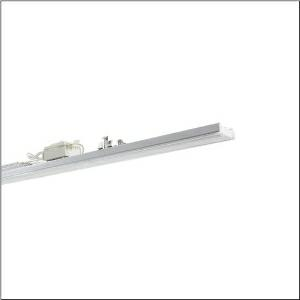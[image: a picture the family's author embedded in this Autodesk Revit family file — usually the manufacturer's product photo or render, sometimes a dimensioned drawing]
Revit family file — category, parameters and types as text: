
# Revit family: licross_r__21_recessed_mo_52te12dv4dxg_0a71
name_source: partatom
category: Lighting Fixtures
units: mm (PartAtom-declared; Revit-internal decimal feet)

## family parameters
Cut with Voids When Loaded = No
Host = Face
Light Source = No
Part Type = Normal
Room Calculation Point = No
Round Connector Dimension = Use Diameter
Shared = No

## types (1)
- --- (1 x LED, 13000 lm, 71 W, 4000K)
    Apparent Load = 71 VA
    CIE Flux Codes = 72 92 99 100 100
    Color Rendering = 80
    Color Temperature = 4000K
    Default Elevation = 1800 mm
    Description = Licross® 21 Recessed MO, luminaire insert, of sheet steel, galvanised, coil coated, white, length: 2.250mm, width: 66mm, height: 67mm, LED rated luminous flux: 13.000lm, light colour: 840, control gear: DALI 2, with plug, 5-pole, with phase selection, mains connection: 220..240V, AC, 50/60Hz, rated input power: 71W, halogen-free wiring, primary optical cover: cover, of PMMA, light emission: direct distribution, primary light characteristic: symmetric, protection rating (complete): IP54, insulation class (complete): insulation class I (protective earthing), certification: CE, ENEC, VDE, UKCA, protection symbol: D if used in an environment with non-conductive dust loads with corresponding accessories, impact resistance: IK06, permissible ambient temperature for indoor applications: -25..+35°C, corresponds to IFS (International Featured Standards) requirements for safety and quality in the food industry, reducing of maximum allowable ambient temperature of 5°C with ceiling mounting, LABS conformity tested according to VDMA 24364:2018-05, packaging unit: 1 piece
    Height = 58 mm
    Lamp = 1 x LED
    Lamp Light Flux = 13000 lm
    Lamp Power = 71 W
    Lamp count = 1
    Length = 2250 mm
    Luminous efficacy = 183 lm/W
    Manufacturer = Siteco
    ModVariant = No
    Model = 52TE12DV4DXG
    Mounting Place = Ceiling
    Mounting Type = Pendant
    Number of Poles = 1
    OnlyDefault = Yes
    Power Factor = 1
    Product Name = Licross® 21 Recessed MO
    Product group = luminaire insert
    ProductGroupID = 902
    Protection Class = Protection class I
    Protection Degree = IP 54
    RLX_Detail_Level = 1
    RLX_Emergency_Light_Flux = 0 lm
    RLX_Emergency_Type = 0
    RLX_Emergency_Type_DB = No
    RlxData = <blob elided: 29505 chars, md5=c9497c53>
    Socket = socket
    Standby Power = 0 W
    System Light Flux = 13000 lm
    System Power = 71 W
    Type Comments = factory setting: luminous flux: 100 % | dim-lin: 254 | 324 mA
    Type Image = l_1296930.jpg
    URL = http://relux.com
    VarID = @adj_126370
    Voltage = 0 V
    Weight = 0.00 kg
    Width = 66 mm

## geometry (parser evidence)
native form markers: Blend x4, Sweep x10
no freeform markers — native parametric forms only
